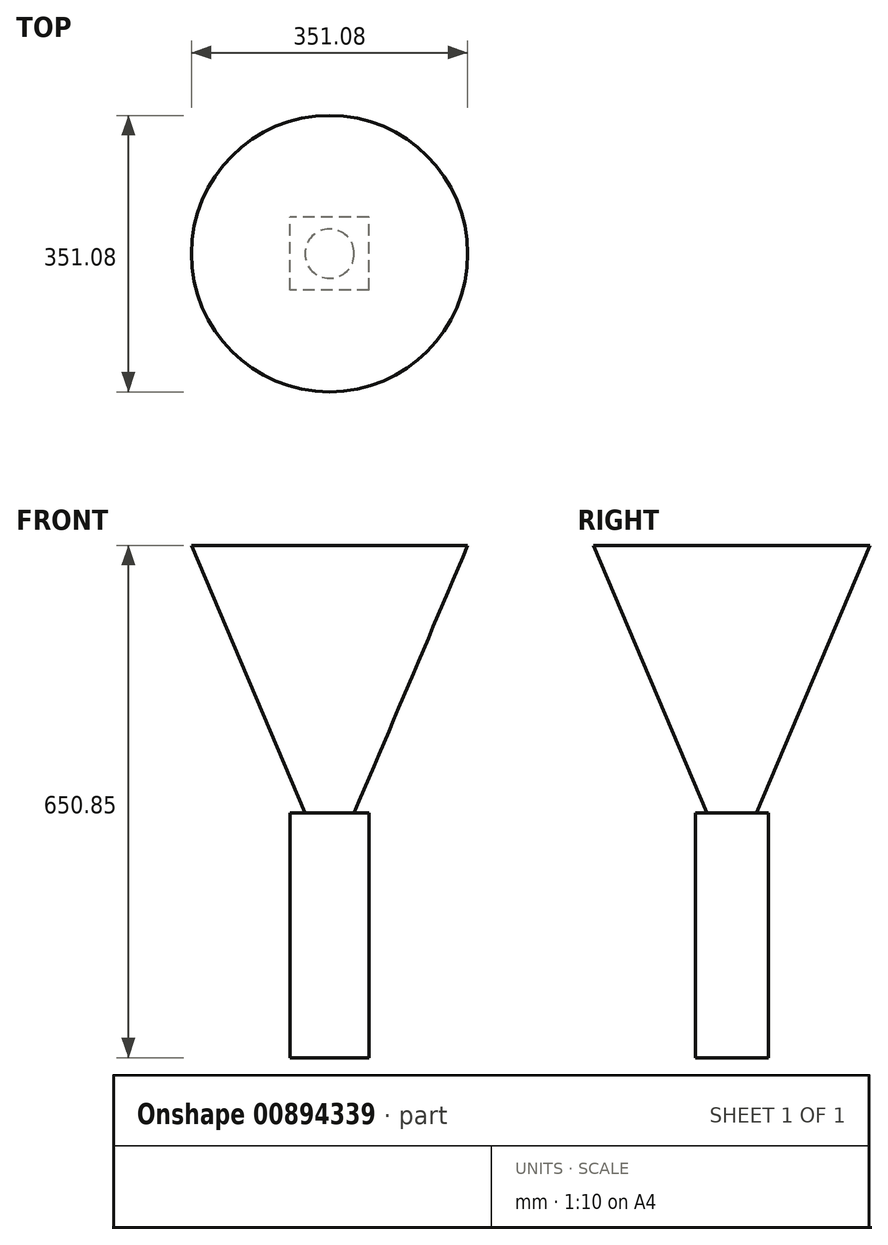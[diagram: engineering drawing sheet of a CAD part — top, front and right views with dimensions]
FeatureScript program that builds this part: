
annotation { "Feature Type Name" : "Feature", "Feature Type Description" : "" }
export const myFeature = defineFeature(function(context is Context, id is Id, definition is map)
    precondition{}
    {
        {
            var Q0;
            Q0=qCreatedBy(makeId("Top.planeOp"),FACE);
            var sketch = newSketch(context, id + "F0", { "sketchPlane" : qUnion([Q0])});
            skLineSegment(sketch, "E0.bottom", {"start": v(50.1, -46.2) * mm, "end": v(-50.1, -46.2) * mm});
            skLineSegment(sketch, "E0.top", {"start": v(50.1, 46.2) * mm, "end": v(-50.1, 46.2) * mm});
            skLineSegment(sketch, "E0.left", {"start": v(50.1, -46.2) * mm, "end": v(50.1, 46.2) * mm});
            skLineSegment(sketch, "E0.right", {"start": v(-50.1, -46.2) * mm, "end": v(-50.1, 46.2) * mm});
            skPoint(sketch, "E0.middle", {"position": v(0, 0) * mm});
            skSolve(sketch);
        }
        {
            var Q0;
            Q0 = qSketchRegion(id + "F0", true);
            extrude(context, id + "F1", {"entities" : qUnion([Q0]), "depth" : 311.15 * mm, "offsetDistance" : 25.4 * mm});
        }
        {
            var Q0;
            Q0=makeQuery(id+"F1.opExtrude","CAP_FACE",FACE,{"disambiguationData":[OSD([sQuery(id+"F0.wireOp",EDGE,"E0.bottom"),sQuery(id+"F0.wireOp",EDGE,"E0.top"),sQuery(id+"F0.wireOp",EDGE,"E0.left"),sQuery(id+"F0.wireOp",EDGE,"E0.right")])],"isStart":false});
            var sketch = newSketch(context, id + "F2", { "sketchPlane" : qUnion([Q0])});
            skCircle(sketch, "E1", {"center": v(0, 0) * mm, "radius": 31.35 * mm});
            skSolve(sketch);
        }
        {
            var Q0;
            Q0=makeQuery(id+"F2.imprint","IMPRINT",FACE,{"disambiguationData":[TD([[makeQuery(id+"F2.imprint","IMPRINT",EDGE,{"derivedFrom":sQuery(id+"F2.wireOp",EDGE,"E1")}),1.0]])]});
            extrude(context, id + "F3", {"entities" : qUnion([Q0]), "operationType" : NewBodyOperationType.ADD, "endBound" : BoundingType.THROUGH_ALL, "depth" : 25.4 * mm, "offsetDistance" : 25.4 * mm, "hasDraft" : true, "draftAngle" : 23 * degree});
        }
    });
